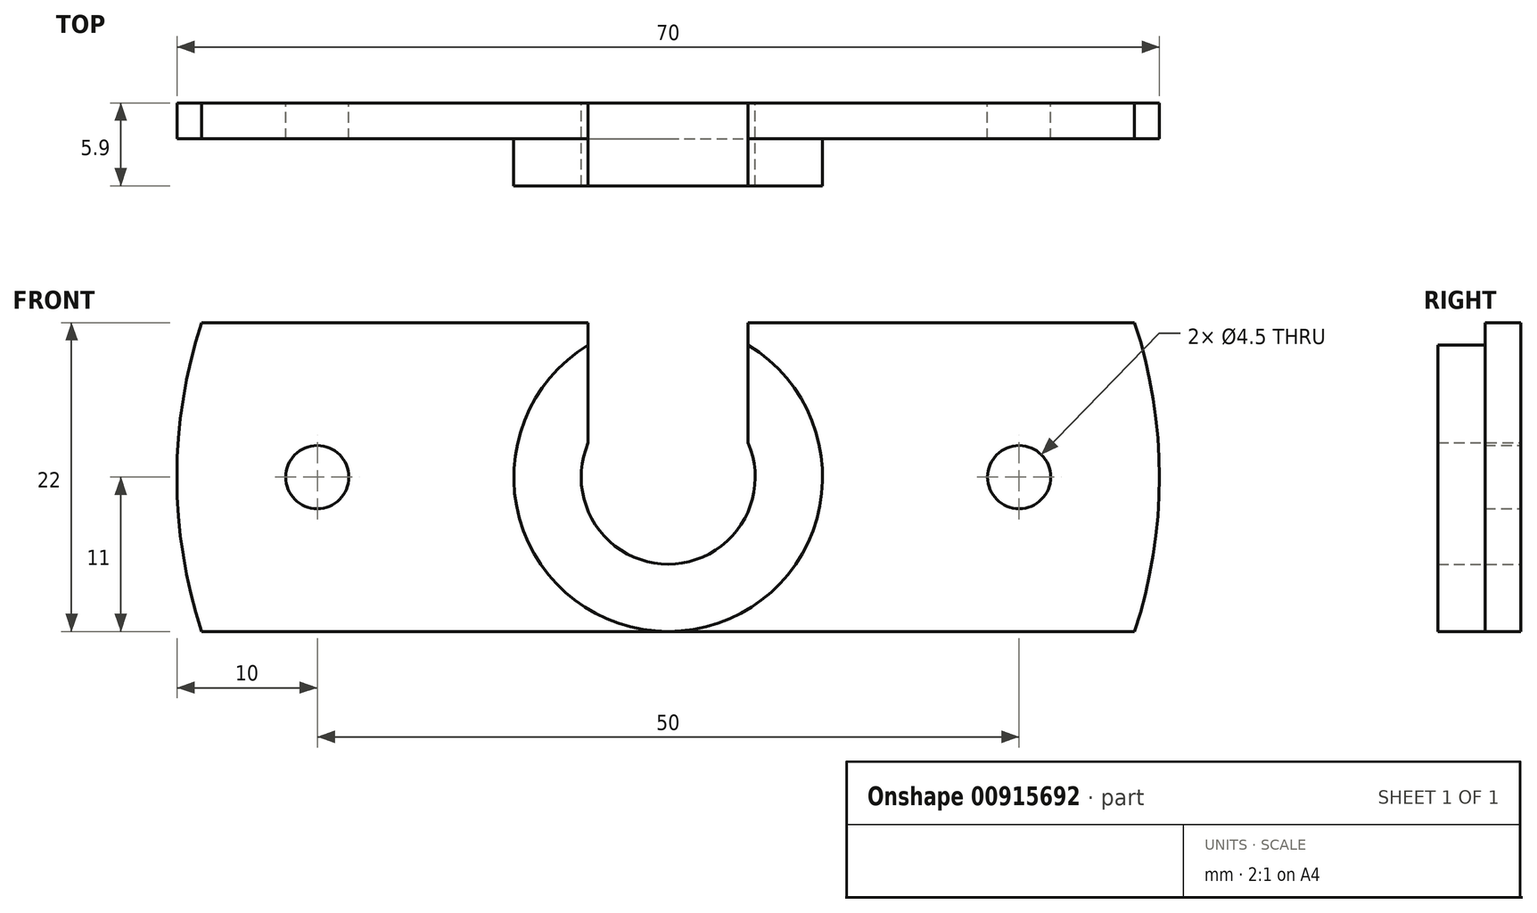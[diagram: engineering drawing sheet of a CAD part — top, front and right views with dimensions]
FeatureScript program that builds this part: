
annotation { "Feature Type Name" : "Feature", "Feature Type Description" : "" }
export const myFeature = defineFeature(function(context is Context, id is Id, definition is map)
    precondition{}
    {
        {
            var Q0;
            Q0=qCreatedBy(makeId("Front.planeOp"),FACE);
            var sketch = newSketch(context, id + "F0", { "sketchPlane" : qUnion([Q0])});
            skCircle(sketch, "E0", {"center": v(-45.91, 41.26) * mm, "radius": 13 * mm});
            skCircle(sketch, "E1", {"center": v(-45.91, 41.26) * mm, "radius": 20 * mm});
            skCircle(sketch, "E2", {"center": v(-45.91, 41.26) * mm, "radius": 28.5 * mm});
            skLineSegment(sketch, "E3", {"start": v(-82.9, 41.26) * mm, "end": v(-10.12, 41.26) * mm, "construction": true});
            skCircle(sketch, "E4", {"center": v(-20.91, 41.26) * mm, "radius": 2.25 * mm});
            skCircle(sketch, "E5", {"center": v(-70.91, 41.26) * mm, "radius": 2.25 * mm});
            skLineSegment(sketch, "E6.0", {"start": v(-70.15, 56.26) * mm, "end": v(-59.14, 56.26) * mm});
            skLineSegment(sketch, "E7.trimOffspring", {"start": v(-32.69, 56.26) * mm, "end": v(-21.68, 56.26) * mm});
            skCircle(sketch, "E8", {"center": v(50, 50) * mm, "radius": 6.2 * mm});
            skCircle(sketch, "E9", {"center": v(50, 50) * mm, "radius": 11 * mm});
            skArc(sketch, "E10", {"start": v(16.77, 61) * mm, "mid": v(15, 50) * mm, "end": v(16.77, 39) * mm});
            skLineSegment(sketch, "E11", {"start": v(13.01, 50) * mm, "end": v(85.8, 50) * mm, "construction": true});
            skCircle(sketch, "E12", {"center": v(75, 50) * mm, "radius": 2.25 * mm});
            skCircle(sketch, "E13", {"center": v(25, 50) * mm, "radius": 2.25 * mm});
            skLineSegment(sketch, "E14.0", {"start": v(13.01, 61) * mm, "end": v(85.8, 61) * mm});
            skLineSegment(sketch, "E15.0", {"start": v(13.01, 39) * mm, "end": v(85.8, 39) * mm});
            skArc(sketch, "E16.trimOffspring", {"start": v(83.23, 39) * mm, "mid": v(85, 50) * mm, "end": v(83.23, 61) * mm});
            skCircle(sketch, "E17", {"center": v(50, 50) * mm, "radius": 8 * mm, "construction": true});
            skLineSegment(sketch, "E18", {"start": v(43.8, 50) * mm, "end": v(43.8, 63.86) * mm});
            skLineSegment(sketch, "E19", {"start": v(56.2, 50) * mm, "end": v(56.2, 63.86) * mm});
            skLineSegment(sketch, "E20", {"start": v(56.2, 63.86) * mm, "end": v(43.8, 63.86) * mm});
            skLineSegment(sketch, "E21.0", {"start": v(55.7, 50) * mm, "end": v(55.7, 63.86) * mm});
            skLineSegment(sketch, "E22.0", {"start": v(44.3, 50) * mm, "end": v(44.3, 63.86) * mm});
            skSolve(sketch);
        }
        {
            var Q0;
            {var subQ0=sQuery(id+"F0.wireOp",EDGE,"E18");var subQ1=sQuery(id+"F0.wireOp",EDGE,"E8");var subQ2=makeQuery(id+"F0.imprint","INTERSECT",VERTEX,{"derivedFrom":[subQ1,subQ0]});Q0=makeQuery(id+"F0.imprint","IMPRINT",FACE,{"disambiguationData":[TD([[makeQuery(id+"F0.imprint","IMPRINT",EDGE,{"disambiguationData":[TD([[subQ2,-1.0]])],"derivedFrom":subQ1}),-1.0]])]});}
            var Q1;
            {var subQ0=sQuery(id+"F0.wireOp",EDGE,"E19");var subQ1=sQuery(id+"F0.wireOp",EDGE,"E8");var subQ2=makeQuery(id+"F0.imprint","INTERSECT",VERTEX,{"derivedFrom":[subQ1,subQ0]});Q1=makeQuery(id+"F0.imprint","IMPRINT",FACE,{"disambiguationData":[TD([[makeQuery(id+"F0.imprint","IMPRINT",EDGE,{"disambiguationData":[TD([[subQ2,-1.0]])],"derivedFrom":subQ1}),-1.0]])]});}
            var Q2;
            {var subQ0=sQuery(id+"F0.wireOp",EDGE,"E18");var subQ1=sQuery(id+"F0.wireOp",EDGE,"E8");var subQ2=makeQuery(id+"F0.imprint","INTERSECT",VERTEX,{"derivedFrom":[subQ1,subQ0]});Q2=makeQuery(id+"F0.imprint","IMPRINT",FACE,{"disambiguationData":[TD([[makeQuery(id+"F0.imprint","IMPRINT",EDGE,{"disambiguationData":[TD([[subQ2,1.0]])],"derivedFrom":subQ1}),-1.0]])]});}
            extrude(context, id + "F1", {"entities" : qUnion([Q0, Q1, Q2]), "depth" : 5.9 * mm, "offsetDistance" : 25 * mm});
        }
        {
            var Q0;
            {var subQ5=sQuery(id+"F0.wireOp",EDGE,"E10");Q0=makeQuery(id+"F0.imprint","IMPRINT",FACE,{"disambiguationData":[TD([[makeQuery(id+"F0.imprint","IMPRINT",EDGE,{"derivedFrom":subQ5}),1.0]])]});}
            var Q1;
            {var subQ0=sQuery(id+"F0.wireOp",EDGE,"E22.0");var subQ1=sQuery(id+"F0.wireOp",EDGE,"E9");var subQ2=makeQuery(id+"F0.imprint","INTERSECT",VERTEX,{"derivedFrom":[subQ1,subQ0]});Q1=makeQuery(id+"F0.imprint","IMPRINT",FACE,{"disambiguationData":[TD([[makeQuery(id+"F0.imprint","IMPRINT",EDGE,{"disambiguationData":[TD([[subQ2,-1.0]])],"derivedFrom":subQ1}),-1.0]])]});}
            var Q2;
            {var subQ0=sQuery(id+"F0.wireOp",EDGE,"E21.0");var subQ1=sQuery(id+"F0.wireOp",EDGE,"E9");var subQ2=makeQuery(id+"F0.imprint","INTERSECT",VERTEX,{"derivedFrom":[subQ1,subQ0]});Q2=makeQuery(id+"F0.imprint","IMPRINT",FACE,{"disambiguationData":[TD([[makeQuery(id+"F0.imprint","IMPRINT",EDGE,{"disambiguationData":[TD([[subQ2,1.0]])],"derivedFrom":subQ1}),-1.0]])]});}
            var Q3;
            Q3=makeQuery(id+"F0.imprint","IMPRINT",FACE,{"disambiguationData":[TD([[makeQuery(id+"F0.imprint","IMPRINT",EDGE,{"derivedFrom":sQuery(id+"F0.wireOp",EDGE,"E12")}),-1.0]])]});
            extrude(context, id + "F2", {"entities" : qUnion([Q0, Q1, Q2, Q3]), "operationType" : NewBodyOperationType.ADD, "depth" : 2.55 * mm, "offsetDistance" : 25 * mm});
        }
    });
